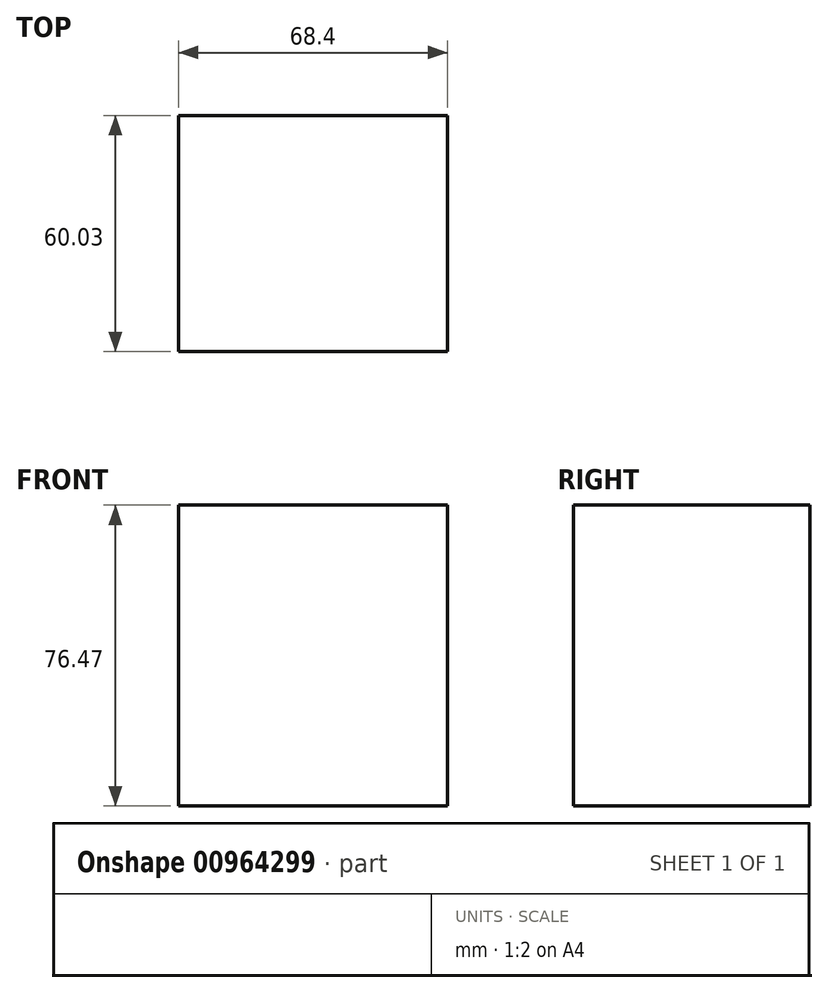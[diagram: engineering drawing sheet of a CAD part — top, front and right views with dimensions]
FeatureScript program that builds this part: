
annotation { "Feature Type Name" : "Feature", "Feature Type Description" : "" }
export const myFeature = defineFeature(function(context is Context, id is Id, definition is map)
    precondition{}
    {
        {
            var Q0;
            Q0=qCreatedBy(makeId("Top.planeOp"),FACE);
            var sketch = newSketch(context, id + "F0", { "sketchPlane" : qUnion([Q0])});
            skLineSegment(sketch, "E0.bottom", {"start": v(68.4, 60.03) * mm, "end": v(0, 60.03) * mm});
            skLineSegment(sketch, "E0.top", {"start": v(68.4, 0) * mm, "end": v(0, 0) * mm});
            skLineSegment(sketch, "E0.left", {"start": v(68.4, 60.03) * mm, "end": v(68.4, 0) * mm});
            skLineSegment(sketch, "E0.right", {"start": v(0, 60.03) * mm, "end": v(0, 0) * mm});
            skLineSegment(sketch, "E1.bottom", {"start": v(0, 30.01) * mm, "end": v(52.92, 30.01) * mm, "construction": true});
            skLineSegment(sketch, "E1.top", {"start": v(0, 0) * mm, "end": v(52.92, 0) * mm, "construction": true});
            skLineSegment(sketch, "E1.left", {"start": v(0, 30.01) * mm, "end": v(0, 0) * mm, "construction": true});
            skLineSegment(sketch, "E1.right", {"start": v(52.92, 30.01) * mm, "end": v(52.92, 0) * mm, "construction": true});
            skSolve(sketch);
        }
        {
            var Q0;
            Q0 = qSketchRegion(id + "F0", true);
            extrude(context, id + "F1", {"entities" : qUnion([Q0]), "depth" : 76.47 * mm, "offsetDistance" : 25.4 * mm});
        }
    });
